# Revit family: TopVent_MC
name_source: partatom
category: Mechanical Equipment
revit_build: Autodesk Revit MEP 2015 (Build: 20160512_0715(x64)
units: mm (PartAtom-declared; Revit-internal decimal feet)

## types (3) — shared parameters
COBIE Condensate quantity 28 °C (8/14 °C) = 0.0/0.0 kg/h
COBIE Connected load = 3.6 kW
COBIE Current consumption max. = 5.9A
COBIE Extract air temperature max. = 50°C
COBIE Frequency = 50 Hz
COBIE Permitted voltage tolerance = +/-5%
COBIE Pressure of the heating medium max. = 800 kPa
COBIE Protection rating = IP 54
COBIE Relative humidity of the fresh air 28 °C (6/12 °C) = 40/60 %
COBIE Relative humidity of the fresh air 32 °C (6/12 °C) = 40/60 %
COBIE Series fuse = 13A
COBIE Static efficiency of the fans = 63.6%
COBIE Supply air temperature max. = 60°C
COBIE Supply voltage = 3x400 V AC
COBIE Temperature of the heating medium max. = 90°C
Condensate quantity 28 °C (8/14 °C) = 0.0/0.0 kg/h
Connected load = 3.6 kW
Current consumption max. = 5.9A
E = 594 mm  [stored 1.94882 ft]
E/2 = 297 mm  [stored 0.974409 ft]
Extract air temperature max. = 50°C
Frequency = 50 Hz
J = 32 mm
K = 1132 mm
M = 32 mm
Permitted voltage tolerance = +/-5%
Pressure of the heating medium max. = 800 kPa
Protection rating = IP 54
Relative humidity of the fresh air 28 °C (6/12 °C) = 40/60 %
Relative humidity of the fresh air 32 °C (6/12 °C) = 40/60 %
Series fuse = 13A
Static efficiency of the fans = 63.6%
Supply air temperature max. = 60°C
Supply voltage = 3x400 V AC
Temperature of the heating medium max. = 90°C

## per-type parameters (varying)
- MC-6-C: A=900 mm  [stored 2.95276 ft]; Air flow rate=3100.0 m3/h; COBIE Air flow rate=3100.0 m3/h; COBIE Condensate quantity=90.0 kg/h; COBIE Condensate quantity 28 °C (6/12 °C)=0.0/0.0 kg/h; COBIE Condensate quantity 32 °C (6/12 °C)=9.7/12.7 kg/h; COBIE Condensate quantity 32 °C (8/14 °C)=4.1/7.1 kg/h; COBIE Effective electric power input=0.85 kW; COBIE Floor area covered=537.0; COBIE Heat output -5/-15 °C (60/40 °C)=45.7/47.2 kW; COBIE Heat output -5/-15 °C (80/60 °C)=76.8/78.2 kW; COBIE Maximum mounting height -5/-15 °C (60/40 °C)=12.3/12.4 m; COBIE Maximum mounting height -5/-15 °C (80/60 °C)=9.7/9.7 m; COBIE Nominal air flow rate=6000.0; COBIE Octave sound power level - 1000 Hz=68 dB; COBIE Octave sound power level - 125 Hz=60 dB; COBIE Octave sound power level - 2000 Hz=68 dB; COBIE Octave sound power level - 250 Hz=63 dB; COBIE Octave sound power level - 4000 Hz=67 dB; COBIE Octave sound power level - 500 Hz=66 dB; COBIE Octave sound power level - 63 Hz=42 dB; COBIE Octave sound power level - 8000 Hz=62 dB; COBIE Sensible cooling capacity 28 °C (6/12 °C)=21.0/20.7 kW; COBIE Sensible cooling capacity 28 °C (8/14 °C)=18.5/18.2 kW; COBIE Sensible cooling capacity 32 °C (6/12 °C)=25.7/25.4 kW; COBIE Sensible cooling capacity 32 °C (8/14 °C)=23.3/23.0 kW; COBIE Sound pressure level (at a distance of 5 m)=52 dB(A); COBIE Supply air temperature -5/-15 °C (60/40 °C)=40.1/39.9 °C; COBIE Supply air temperature -5/-15 °C (80/60 °C)=55.5/55.2 °C; COBIE Supply air temperature 28 °C (6/12 °C)=14.0/14.2 kW; COBIE Supply air temperature 28 °C (8/14 °C)=15.2/15.4 °C; COBIE Supply air temperature 32 °C (6/12 °C)=15.7/15.8 kW; COBIE Supply air temperature 32 °C (8/14 °C)=16.9/17.0 °C; COBIE Total cooling capacity 28 °C (6/12 °C)=21.0/20.7 kW; COBIE Total cooling capacity 28 °C (8/14 °C)=18.5/18.2 kW; COBIE Total cooling capacity 32 °C (6/12 °C)=32.3/34.1 kW; COBIE Total cooling capacity 32 °C (8/14 °C)=26.1/27.8 kW; COBIE Total sound power level=74 dB(A); COBIE Water content of heating coil=4.6 l; COBIE Water pressure drop -5/-15 °C (60/40 °C)=7/7 kPa; COBIE Water pressure drop -5/-15 °C (80/60 °C)=18/19 kPa; COBIE Water pressure drop 28 °C (6/12 °C)=16/16 kW; COBIE Water pressure drop 28 °C (8/14 °C)=13/12 kPa; COBIE Water pressure drop 32 °C (6/12 °C)=39/43 kW; COBIE Water pressure drop 32 °C (8/14 °C)=25/29 kPa; COBIE Water quantity -5/-15 °C (60/40 °C)=1965/2026 l/h; COBIE Water quantity -5/-15 °C (80/60 °C)=3297/3358 l/h; COBIE Water quantity 28 °C (6/12 °C)=3000/2961 l/h; COBIE Water quantity 28 °C (8/14 °C)=2649/2609 l/h; COBIE Water quantity 32 °C (6/12 °C)=4630/4884 l/h; COBIE Water quantity 32 °C (8/14 °C)=3734/3988 l/h; COBIE Weight=165 kg; Condensate quantity=90.0 kg/h; Condensate quantity 28 °C (6/12 °C)=0.0/0.0 kg/h; Condensate quantity 32 °C (6/12 °C)=9.7/12.7 kg/h; Condensate quantity 32 °C (8/14 °C)=4.1/7.1 kg/h; Effective electric power input=0.85 kW; F=758 mm  [stored 2.48688 ft]; Floor area covered=537 m²; G=910 mm; H=832 mm; Heat output -5/-15 °C (60/40 °C)=45.7/47.2 kW; Heat output -5/-15 °C (80/60 °C)=76.8/78.2 kW; I=760 mm  [stored 2.49344 ft]; Maximum mounting height -5/-15 °C (60/40 °C)=12.3/12.4 m; Maximum mounting height -5/-15 °C (80/60 °C)=9.7/9.7 m; Nominal air flow rate=6000 m³/h; O=420 mm  [stored 1.37795 ft]; Octave sound power level - 1000 Hz=68 dB; Octave sound power level - 125 Hz=60 dB; Octave sound power level - 2000 Hz=68 dB; Octave sound power level - 250 Hz=63 dB; Octave sound power level - 4000 Hz=67 dB; Octave sound power level - 500 Hz=66 dB; Octave sound power level - 63 Hz=42 dB; Octave sound power level - 8000 Hz=62 dB; P=850 mm  [stored 2.78871 ft]; R=2100 mm; Sensible cooling capacity 28 °C (6/12 °C)=21.0/20.7 kW; Sensible cooling capacity 28 °C (8/14 °C)=18.5/18.2 kW; Sensible cooling capacity 32 °C (6/12 °C)=25.7/25.4 kW; Sensible cooling capacity 32 °C (8/14 °C)=23.3/23.0 kW; Sound pressure level (at a distance of 5 m)=52 dB(A); Supply air temperature -5/-15 °C (60/40 °C)=40.1/39.9 °C; Supply air temperature -5/-15 °C (80/60 °C)=55.5/55.2 °C; Supply air temperature 28 °C (6/12 °C)=14.0/14.2 kW; Supply air temperature 28 °C (8/14 °C)=15.2/15.4 °C; Supply air temperature 32 °C (6/12 °C)=15.7/15.8 kW; Supply air temperature 32 °C (8/14 °C)=16.9/17.0 °C; Total cooling capacity 28 °C (6/12 °C)=21.0/20.7 kW; Total cooling capacity 28 °C (8/14 °C)=18.5/18.2 kW; Total cooling capacity 32 °C (6/12 °C)=32.3/34.1 kW; Total cooling capacity 32 °C (8/14 °C)=26.1/27.8 kW; Total sound power level=74 dB(A); U=1020 mm  [stored 3.34646 ft]; Water content of heating coil=4.6 l; Water pressure drop -5/-15 °C (60/40 °C)=7/7 kPa; Water pressure drop -5/-15 °C (80/60 °C)=18/19 kPa; Water pressure drop 28 °C (6/12 °C)=16/16 kW; Water pressure drop 28 °C (8/14 °C)=13/12 kPa; Water pressure drop 32 °C (6/12 °C)=39/43 kW; Water pressure drop 32 °C (8/14 °C)=25/29 kPa; Water quantity -5/-15 °C (60/40 °C)=1965/2026 l/h; Water quantity -5/-15 °C (80/60 °C)=3297/3358 l/h; Water quantity 28 °C (6/12 °C)=3000/2961 l/h; Water quantity 28 °C (8/14 °C)=2649/2609 l/h; Water quantity 32 °C (6/12 °C)=4630/4884 l/h; Water quantity 32 °C (8/14 °C)=3734/3988 l/h; Weight=165 kg
- MC-9-C: A=1100 mm; Air flow rate=5000.0 m3/h; COBIE Air flow rate=5000.0 m3/h; COBIE Condensate quantity=150.0 kg/h; COBIE Condensate quantity 28 °C (6/12 °C)=0.0/0.0 kg/h; COBIE Condensate quantity 32 °C (6/12 °C)=18.0/22.7 kg/h; COBIE Condensate quantity 32 °C (8/14 °C)=0.0/4.0 kg/h; COBIE Effective electric power input=1.44 kW; COBIE Floor area covered=946.0; COBIE Heat output -5/-15 °C (60/40 °C)=71.0/73.2 kW; COBIE Heat output -5/-15 °C (80/60 °C)=119.0/121.2 kW; COBIE Maximum mounting height -5/-15 °C (60/40 °C)=12.9/12.9 m; COBIE Maximum mounting height -5/-15 °C (80/60 °C)=10.1/10.1 m; COBIE Nominal air flow rate=9000.0; COBIE Octave sound power level - 1000 Hz=75 dB; COBIE Octave sound power level - 125 Hz=67 dB; COBIE Octave sound power level - 2000 Hz=75 dB; COBIE Octave sound power level - 250 Hz=70 dB; COBIE Octave sound power level - 4000 Hz=74 dB; COBIE Octave sound power level - 500 Hz=73 dB; COBIE Octave sound power level - 63 Hz=49 dB; COBIE Octave sound power level - 8000 Hz=68 dB; COBIE Sensible cooling capacity 28 °C (6/12 °C)=32.2/31.8 kW; COBIE Sensible cooling capacity 28 °C (8/14 °C)=28.4/28.0 kW; COBIE Sensible cooling capacity 32 °C (6/12 °C)=39.7/39.3 kW; COBIE Sensible cooling capacity 32 °C (8/14 °C)=35.8/35.4 kW; COBIE Sound pressure level (at a distance of 5 m)=59 dB(A); COBIE Supply air temperature -5/-15 °C (60/40 °C)=40.9/40.7 °C; COBIE Supply air temperature -5/-15 °C (80/60 °C)=56.8/56.5 °C; COBIE Supply air temperature 28 °C (6/12 °C)=13.8/13.9 kW; COBIE Supply air temperature 28 °C (8/14 °C)=15.0/15.2 °C; COBIE Supply air temperature 32 °C (6/12 °C)=15.3/15.4 kW; COBIE Supply air temperature 32 °C (8/14 °C)=16.6/16.7 °C; COBIE Total cooling capacity 28 °C (6/12 °C)=32.2/31.8 kW; COBIE Total cooling capacity 28 °C (8/14 °C)=28.4/28.0 kW; COBIE Total cooling capacity 32 °C (6/12 °C)=51.9/54.7 kW; COBIE Total cooling capacity 32 °C (8/14 °C)=35.8/38.1 kW; COBIE Total sound power level=81 dB(A); COBIE Water content of heating coil=4.6 l; COBIE Water pressure drop -5/-15 °C (60/40 °C)=7/7 kPa; COBIE Water pressure drop -5/-15 °C (80/60 °C)=18/19 kPa; COBIE Water pressure drop 28 °C (6/12 °C)=16/16 kW; COBIE Water pressure drop 28 °C (8/14 °C)=12/12 kPa; COBIE Water pressure drop 32 °C (6/12 °C)=41/46 kW; COBIE Water pressure drop 32 °C (8/14 °C)=20/22 kPa; COBIE Water quantity -5/-15 °C (60/40 °C)=3050/3145 l/h; COBIE Water quantity -5/-15 °C (80/60 °C)=5113/5208 l/h; COBIE Water quantity 28 °C (6/12 °C)=4614/4554 l/h; COBIE Water quantity 28 °C (8/14 °C)=4064/4004 l/h; COBIE Water quantity 32 °C (6/12 °C)=7432/7829 l/h; COBIE Water quantity 32 °C (8/14 °C)=5131/5459 l/h; COBIE Weight=165 kg; Condensate quantity=150.0 kg/h; Condensate quantity 28 °C (6/12 °C)=0.0/0.0 kg/h; Condensate quantity 32 °C (6/12 °C)=18.0/22.7 kg/h; Condensate quantity 32 °C (8/14 °C)=0.0/4.0 kg/h; Effective electric power input=1.44 kW; F=882 mm  [stored 2.8937 ft]; Floor area covered=946 m²; G=931 mm  [stored 3.05446 ft]; H=853 mm  [stored 2.79856 ft]; Heat output -5/-15 °C (60/40 °C)=71.0/73.2 kW; Heat output -5/-15 °C (80/60 °C)=119.0/121.2 kW; I=935 mm; Maximum mounting height -5/-15 °C (60/40 °C)=12.9/12.9 m; Maximum mounting height -5/-15 °C (80/60 °C)=10.1/10.1 m; Nominal air flow rate=9000 m³/h; O=500 mm  [stored 1.64042 ft]; Octave sound power level - 1000 Hz=75 dB; Octave sound power level - 125 Hz=67 dB; Octave sound power level - 2000 Hz=75 dB; Octave sound power level - 250 Hz=70 dB; Octave sound power level - 4000 Hz=74 dB; Octave sound power level - 500 Hz=73 dB; Octave sound power level - 63 Hz=49 dB; Octave sound power level - 8000 Hz=68 dB; P=1050 mm; R=2190 mm  [stored 7.18504 ft]; Sensible cooling capacity 28 °C (6/12 °C)=32.2/31.8 kW; Sensible cooling capacity 28 °C (8/14 °C)=28.4/28.0 kW; Sensible cooling capacity 32 °C (6/12 °C)=39.7/39.3 kW; Sensible cooling capacity 32 °C (8/14 °C)=35.8/35.4 kW; Sound pressure level (at a distance of 5 m)=59 dB(A); Supply air temperature -5/-15 °C (60/40 °C)=40.9/40.7 °C; Supply air temperature -5/-15 °C (80/60 °C)=56.8/56.5 °C; Supply air temperature 28 °C (6/12 °C)=13.8/13.9 kW; Supply air temperature 28 °C (8/14 °C)=15.0/15.2 °C; Supply air temperature 32 °C (6/12 °C)=15.3/15.4 kW; Supply air temperature 32 °C (8/14 °C)=16.6/16.7 °C; Total cooling capacity 28 °C (6/12 °C)=32.2/31.8 kW; Total cooling capacity 28 °C (8/14 °C)=28.4/28.0 kW; Total cooling capacity 32 °C (6/12 °C)=51.9/54.7 kW; Total cooling capacity 32 °C (8/14 °C)=35.8/38.1 kW; Total sound power level=81 dB(A); U=1220 mm  [stored 4.00262 ft]; Water content of heating coil=4.6 l; Water pressure drop -5/-15 °C (60/40 °C)=7/7 kPa; Water pressure drop -5/-15 °C (80/60 °C)=18/19 kPa; Water pressure drop 28 °C (6/12 °C)=16/16 kW; Water pressure drop 28 °C (8/14 °C)=12/12 kPa; Water pressure drop 32 °C (6/12 °C)=41/46 kW; Water pressure drop 32 °C (8/14 °C)=20/22 kPa; Water quantity -5/-15 °C (60/40 °C)=3050/3145 l/h; Water quantity -5/-15 °C (80/60 °C)=5113/5208 l/h; Water quantity 28 °C (6/12 °C)=4614/4554 l/h; Water quantity 28 °C (8/14 °C)=4064/4004 l/h; Water quantity 32 °C (6/12 °C)=7432/7829 l/h; Water quantity 32 °C (8/14 °C)=5131/5459 l/h; Weight=165 kg
- MC-9-D: A=1100 mm; Air flow rate=5000.0 m3/h; COBIE Air flow rate=5000.0 m3/h; COBIE Condensate quantity=150.0 kg/h; COBIE Condensate quantity 28 °C (6/12 °C)=0.0/0.1 kg/h; COBIE Condensate quantity 32 °C (6/12 °C)=25.6/31.2 kg/h; COBIE Condensate quantity 32 °C (8/14 °C)=15.7/21.3 kg/h; COBIE Effective electric power input=1.56 kW; COBIE Floor area covered=946.0; COBIE Heat output -5/-15 °C (60/40 °C)=86.7/89.3 kW; COBIE Heat output -5/-15 °C (80/60 °C)=142.0/144.6 kW; COBIE Maximum mounting height -5/-15 °C (60/40 °C)=11.7/11.7 m; COBIE Maximum mounting height -5/-15 °C (80/60 °C)=9.3/9.4 m; COBIE Nominal air flow rate=9000.0; COBIE Octave sound power level - 1000 Hz=75 dB; COBIE Octave sound power level - 125 Hz=67 dB; COBIE Octave sound power level - 2000 Hz=75 dB; COBIE Octave sound power level - 250 Hz=70 dB; COBIE Octave sound power level - 4000 Hz=74 dB; COBIE Octave sound power level - 500 Hz=73 dB; COBIE Octave sound power level - 63 Hz=49 dB; COBIE Octave sound power level - 8000 Hz=68 dB; COBIE Sensible cooling capacity 28 °C (6/12 °C)=38.1/37.7 kW; COBIE Sensible cooling capacity 28 °C (8/14 °C)=33.2/32.9 kW; COBIE Sensible cooling capacity 32 °C (6/12 °C)=47.4/47.1 kW; COBIE Sensible cooling capacity 32 °C (8/14 °C)=42.6/42.2 kW; COBIE Sound pressure level (at a distance of 5 m)=59 dB(A); COBIE Supply air temperature -5/-15 °C (60/40 °C)=46.1/46.0 °C; COBIE Supply air temperature -5/-15 °C (80/60 °C)=64.4/64.2 °C; COBIE Supply air temperature 28 °C (6/12 °C)=11.8/12.0 kW; COBIE Supply air temperature 28 °C (8/14 °C)=13.4/13.6 °C; COBIE Supply air temperature 32 °C (6/12 °C)=12.7/12.9 kW; COBIE Supply air temperature 32 °C (8/14 °C)=14.3/14.5 °C; COBIE Total cooling capacity 28 °C (6/12 °C)=38.1/37.8 kW; COBIE Total cooling capacity 28 °C (8/14 °C)=33.2/32.9 kW; COBIE Total cooling capacity 32 °C (6/12 °C)=64.8/68.3 kW; COBIE Total cooling capacity 32 °C (8/14 °C)=53.3/56.7 kW; COBIE Total sound power level=81 dB(A); COBIE Water content of heating coil=7.9 l; COBIE Water pressure drop -5/-15 °C (60/40 °C)=6/6 kPa; COBIE Water pressure drop -5/-15 °C (80/60 °C)=15/15 kPa; COBIE Water pressure drop 28 °C (6/12 °C)=13/13 kW; COBIE Water pressure drop 28 °C (8/14 °C)=10/10 kPa; COBIE Water pressure drop 32 °C (6/12 °C)=39/43 kW; COBIE Water pressure drop 32 °C (8/14 °C)=26/30 kPa; COBIE Water quantity -5/-15 °C (60/40 °C)=3725/3837 l/h; COBIE Water quantity -5/-15 °C (80/60 °C)=6101/6212 l/h; COBIE Water quantity 28 °C (6/12 °C)=5451/5409 l/h; COBIE Water quantity 28 °C (8/14 °C)=4756/4706 l/h; COBIE Water quantity 32 °C (6/12 °C)=9285/9785 l/h; COBIE Water quantity 32 °C (8/14 °C)=7626/8126 l/h; COBIE Weight=172 kg; Condensate quantity=150.0 kg/h; Condensate quantity 28 °C (6/12 °C)=0.0/0.1 kg/h; Condensate quantity 32 °C (6/12 °C)=25.6/31.2 kg/h; Condensate quantity 32 °C (8/14 °C)=15.7/21.3 kg/h; Effective electric power input=1.56 kW; F=882 mm  [stored 2.8937 ft]; Floor area covered=946 m²; G=940 mm  [stored 3.08399 ft]; H=845 mm  [stored 2.77231 ft]; Heat output -5/-15 °C (60/40 °C)=86.7/89.3 kW; Heat output -5/-15 °C (80/60 °C)=142.0/144.6 kW; I=935 mm; Maximum mounting height -5/-15 °C (60/40 °C)=11.7/11.7 m; Maximum mounting height -5/-15 °C (80/60 °C)=9.3/9.4 m; Nominal air flow rate=9000 m³/h; O=500 mm  [stored 1.64042 ft]; Octave sound power level - 1000 Hz=75 dB; Octave sound power level - 125 Hz=67 dB; Octave sound power level - 2000 Hz=75 dB; Octave sound power level - 250 Hz=70 dB; Octave sound power level - 4000 Hz=74 dB; Octave sound power level - 500 Hz=73 dB; Octave sound power level - 63 Hz=49 dB; Octave sound power level - 8000 Hz=68 dB; P=1050 mm; R=2190 mm  [stored 7.18504 ft]; Sensible cooling capacity 28 °C (6/12 °C)=38.1/37.7 kW; Sensible cooling capacity 28 °C (8/14 °C)=33.2/32.9 kW; Sensible cooling capacity 32 °C (6/12 °C)=47.4/47.1 kW; Sensible cooling capacity 32 °C (8/14 °C)=42.6/42.2 kW; Sound pressure level (at a distance of 5 m)=59 dB(A); Supply air temperature -5/-15 °C (60/40 °C)=46.1/46.0 °C; Supply air temperature -5/-15 °C (80/60 °C)=64.4/64.2 °C; Supply air temperature 28 °C (6/12 °C)=11.8/12.0 kW; Supply air temperature 28 °C (8/14 °C)=13.4/13.6 °C; Supply air temperature 32 °C (6/12 °C)=12.7/12.9 kW; Supply air temperature 32 °C (8/14 °C)=14.3/14.5 °C; Total cooling capacity 28 °C (6/12 °C)=38.1/37.8 kW; Total cooling capacity 28 °C (8/14 °C)=33.2/32.9 kW; Total cooling capacity 32 °C (6/12 °C)=64.8/68.3 kW; Total cooling capacity 32 °C (8/14 °C)=53.3/56.7 kW; Total sound power level=81 dB(A); U=1220 mm  [stored 4.00262 ft]; Water content of heating coil=7.9 l; Water pressure drop -5/-15 °C (60/40 °C)=6/6 kPa; Water pressure drop -5/-15 °C (80/60 °C)=15/15 kPa; Water pressure drop 28 °C (6/12 °C)=13/13 kW; Water pressure drop 28 °C (8/14 °C)=10/10 kPa; Water pressure drop 32 °C (6/12 °C)=39/43 kW; Water pressure drop 32 °C (8/14 °C)=26/30 kPa; Water quantity -5/-15 °C (60/40 °C)=3725/3837 l/h; Water quantity -5/-15 °C (80/60 °C)=6101/6212 l/h; Water quantity 28 °C (6/12 °C)=5451/5409 l/h; Water quantity 28 °C (8/14 °C)=4756/4706 l/h; Water quantity 32 °C (6/12 °C)=9285/9785 l/h; Water quantity 32 °C (8/14 °C)=7626/8126 l/h; Weight=172 kg

note: [stored X ft] marks values corroborated as IEEE doubles in the binary element streams (Revit-internal decimal feet)

## geometry (parser evidence)
native form markers: Blend x2, Sweep x9
no freeform markers — native parametric forms only
